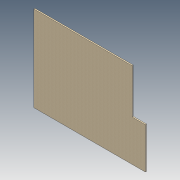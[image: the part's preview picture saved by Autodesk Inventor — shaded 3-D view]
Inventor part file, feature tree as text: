
AUTODESK INVENTOR PART (.ipt)
format: ipt  version: 2012 (Build 160160000, 160)  size: 80,384 bytes
history: native  units: in
note: dims shown in document units (in); Inventor stores cm internally (conversion verified against a paired STEP export)
features: extrude x1, sketch x1
ambient origin geometry x8: Origin, YZ Plane, XZ Plane, XY Plane, X Axis, Y Axis, Z Axis, Center Point
bodies: Solid1 (feature_tree)
feature tree (2):
  extrude  "Extrusion1"  Depth=38.5in
  sketch  "Sketch1"  dims[d0=50.25in d1=38.5in d2=44.25in d3=20.0in d4=0.5in d5=0.0in]
